# Revit family: Lighting-Surface-Amerlux-Stadia
name_source: partatom
category: Lighting Fixtures
units: mm (PartAtom-declared; Revit-internal decimal feet)

## family parameters
Cut with Voids When Loaded = No
Host = Face
Light Source = Yes
Part Type = Normal
Room Calculation Point = No
Round Connector Dimension = Use Diameter
Shared = No

## types (2) — shared parameters
Apparent Load = 0 VA
Color Filter = 16777215
Default Elevation = 48"
Description = Surface Mount
Dimming Lamp Color Temperature Shift = <None>
Emit Shape Visible in Rendering = No
Fixture Finish = Matte Black
Height = 4 7/16"
Manufacturer = Amerlux
Model = Stadia
Number of Poles = 1
Photometric Web File = Load File
Power Factor = 1
Tilt Angle = -90.00°
URL = http://www.amerlux.com
Voltage = 0 V

## per-type parameters (varying)
| type | Aperture | Bottom Offset | Fixture Length | Fixture Width | Side Offset |
| 8" | 8 1/4" | 4 11/16" | 13 3/16" | 10 15/16" | 5 1/2" |
| 5" | 5" | 4" | 11 1/2" | 7 3/4" | 3 7/8" |

note: column(s) folded — value = type name in every type: Emit from Rectangle Length, Emit from Rectangle Width

## geometry (parser evidence)
native form markers: Sweep x5
no freeform markers — native parametric forms only
